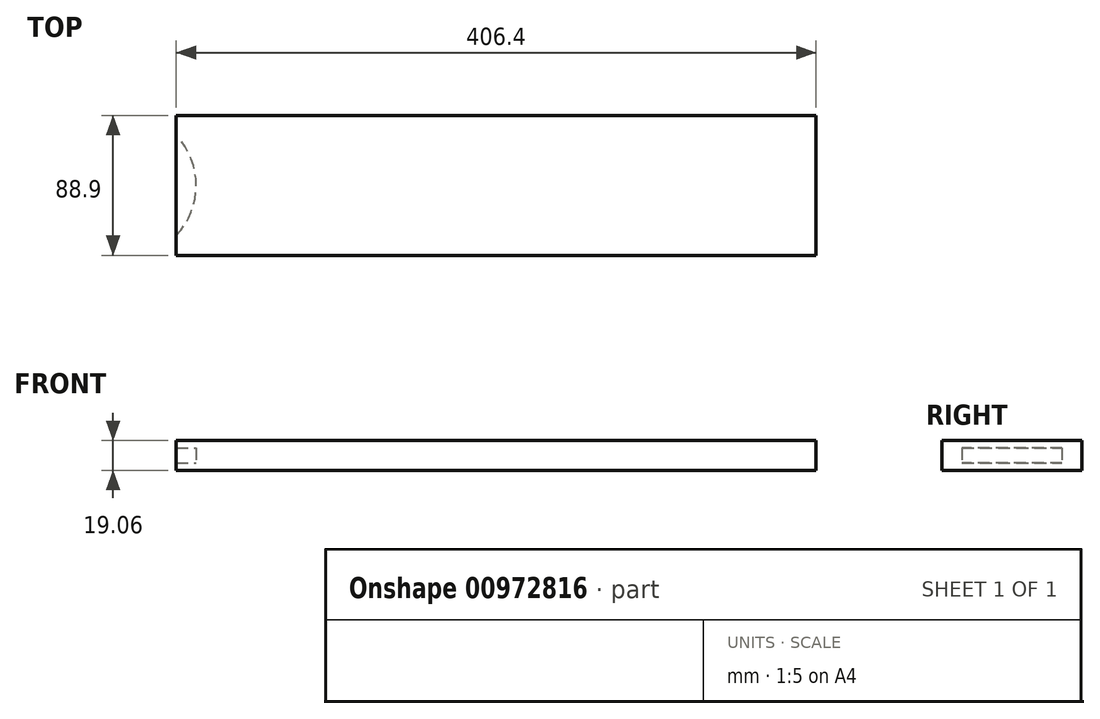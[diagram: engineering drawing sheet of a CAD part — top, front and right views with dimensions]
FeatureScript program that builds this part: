
annotation { "Feature Type Name" : "Feature", "Feature Type Description" : "" }
export const myFeature = defineFeature(function(context is Context, id is Id, definition is map)
    precondition{}
    {
        {
            var Q0;
            Q0=qCreatedBy(makeId("Right.planeOp"),FACE);
            var sketch = newSketch(context, id + "F0", { "sketchPlane" : qUnion([Q0])});
            skLineSegment(sketch, "E0.bottom", {"start": v(44.45, 9.53) * mm, "end": v(-44.45, 9.53) * mm});
            skLineSegment(sketch, "E0.top", {"start": v(44.45, -9.53) * mm, "end": v(-44.45, -9.53) * mm});
            skLineSegment(sketch, "E0.left", {"start": v(44.45, 9.53) * mm, "end": v(44.45, -9.53) * mm});
            skLineSegment(sketch, "E0.right", {"start": v(-44.45, 9.53) * mm, "end": v(-44.45, -9.53) * mm});
            skPoint(sketch, "E0.middle", {"position": v(0, 0) * mm});
            skSolve(sketch);
        }
        {
            var Q0;
            Q0=makeQuery(id+"F0.imprint","IMPRINT",FACE,{"disambiguationData":[TD([[makeQuery(id+"F0.imprint","IMPRINT",EDGE,{"derivedFrom":sQuery(id+"F0.wireOp",EDGE,"E0.bottom")}),1.0]])]});
            extrude(context, id + "F1", {"entities" : qUnion([Q0]), "depth" : 406.4 * mm, "offsetDistance" : 25.4 * mm});
        }
        {
            var Q0;
            Q0=qCreatedBy(makeId("Top.planeOp"),FACE);
            var sketch = newSketch(context, id + "F2", { "sketchPlane" : qUnion([Q0])});
            skArc(sketch, "E1", {"start": v(0, -31.75) * mm, "mid": v(12.7, 0) * mm, "end": v(0, 31.75) * mm});
            skLineSegment(sketch, "E2", {"start": v(-47.78, 0) * mm, "end": v(120.51, 0) * mm, "construction": true});
            skLineSegment(sketch, "E3", {"start": v(0, 31.75) * mm, "end": v(0, -31.75) * mm});
            skSolve(sketch);
        }
        {
            var Q0;
            Q0=qSketchRegion(id+"F2",true);
            extrude(context, id + "F3", {"entities" : qUnion([Q0]), "operationType" : NewBodyOperationType.REMOVE, "depth" : 4.76 * mm, "offsetDistance" : 25.4 * mm, "hasSecondDirection" : true, "secondDirectionOppositeDirection" : true, "secondDirectionDepth" : 4.76 * mm});
        }
        {
            var Q0;
            Q0=makeQuery(id+"F1.opExtrude","CAP_FACE",FACE,{"disambiguationData":[OSD([sQuery(id+"F0.wireOp",EDGE,"E0.bottom"),sQuery(id+"F0.wireOp",EDGE,"E0.top"),sQuery(id+"F0.wireOp",EDGE,"E0.left"),sQuery(id+"F0.wireOp",EDGE,"E0.right")])],"isStart":true});
            var Q1;
            Q1=makeQuery(id+"F1.opExtrude","CAP_FACE",FACE,{"disambiguationData":[OSD([sQuery(id+"F0.wireOp",EDGE,"E0.bottom"),sQuery(id+"F0.wireOp",EDGE,"E0.top"),sQuery(id+"F0.wireOp",EDGE,"E0.left"),sQuery(id+"F0.wireOp",EDGE,"E0.right")])],"isStart":false});
            cPlane(context, id + "F4", {"entities" : qUnion([Q0, Q1]), "cplaneType" : CPlaneType.MID_PLANE, "offset" : 25.4 * mm, "width" : 152.4 * mm, "height" : 152.4 * mm});
        }
    });
